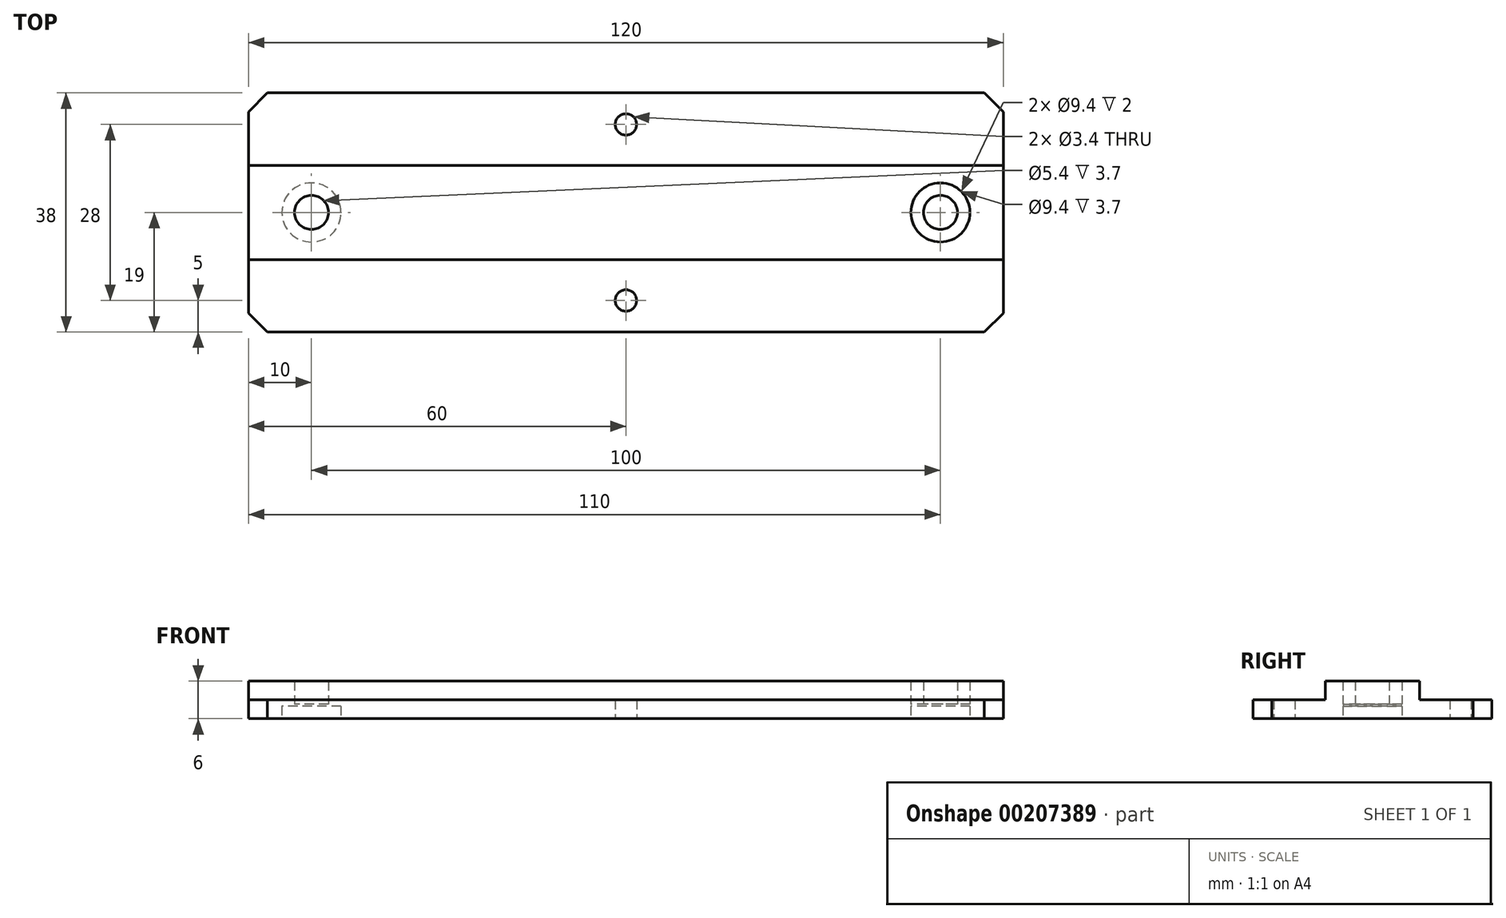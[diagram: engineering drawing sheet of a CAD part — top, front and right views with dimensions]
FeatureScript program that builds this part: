
annotation { "Feature Type Name" : "Feature", "Feature Type Description" : "" }
export const myFeature = defineFeature(function(context is Context, id is Id, definition is map)
    precondition{}
    {
        {
            var Q0;
            Q0=qCreatedBy(makeId("Top.planeOp"),FACE);
            var sketch = newSketch(context, id + "F0", { "sketchPlane" : qUnion([Q0])});
            skLineSegment(sketch, "E0.bottom", {"start": v(-12.5, 19) * mm, "end": v(12.5, 19) * mm});
            skLineSegment(sketch, "E0.top", {"start": v(-8.92, -19) * mm, "end": v(16.08, -19) * mm});
            skPoint(sketch, "E1", {"position": v(0, 19) * mm});
            skPoint(sketch, "E2.rect.middle", {"position": v(-50, 0) * mm});
            skCircle(sketch, "E3", {"center": v(-50, 0) * mm, "radius": 2.7 * mm});
            skCircle(sketch, "E4", {"center": v(-50, 0) * mm, "radius": 4.7 * mm});
            skLineSegment(sketch, "E5", {"start": v(-12.5, 7.5) * mm, "end": v(12.5, 7.5) * mm});
            skLineSegment(sketch, "E6", {"start": v(-12.5, -7.5) * mm, "end": v(12.5, -7.5) * mm});
            skPoint(sketch, "E7", {"position": v(12.5, 0) * mm});
            skLineSegment(sketch, "E8", {"start": v(5.33, 7.5) * mm, "end": v(5.33, -7.5) * mm, "construction": true});
            skPoint(sketch, "E9", {"position": v(5.33, 0) * mm});
            skCircle(sketch, "E10", {"center": v(0, 14) * mm, "radius": 1.7 * mm});
            skCircle(sketch, "E11", {"center": v(0, -14) * mm, "radius": 1.7 * mm});
            skLineSegment(sketch, "E12", {"start": v(0, 14) * mm, "end": v(0, 14) * mm});
            skLineSegment(sketch, "E13", {"start": v(-12.5, 19) * mm, "end": v(-60, 19) * mm});
            skLineSegment(sketch, "E14", {"start": v(-8.92, -19) * mm, "end": v(-60, -19) * mm});
            skLineSegment(sketch, "E15", {"start": v(-60, -19) * mm, "end": v(-60, 19) * mm});
            skLineSegment(sketch, "E16", {"start": v(-12.5, 7.5) * mm, "end": v(-60, 7.5) * mm});
            skLineSegment(sketch, "E17", {"start": v(-12.5, -7.5) * mm, "end": v(-60, -7.5) * mm});
            skLineSegment(sketch, "E18.MirrorCS", {"start": v(12.5, 19) * mm, "end": v(60, 19) * mm});
            skLineSegment(sketch, "E19.MirrorCS", {"start": v(12.5, 7.5) * mm, "end": v(60, 7.5) * mm});
            skLineSegment(sketch, "E20.MirrorCS", {"start": v(12.5, -7.5) * mm, "end": v(60, -7.5) * mm});
            skLineSegment(sketch, "E21.MirrorCS", {"start": v(60, -19) * mm, "end": v(60, 19) * mm});
            skLineSegment(sketch, "E22.MirrorCS", {"start": v(8.92, -19) * mm, "end": v(60, -19) * mm});
            skPoint(sketch, "E23.MirrorP", {"position": v(50, 0) * mm});
            skCircle(sketch, "E24.MirrorC", {"center": v(50, 0) * mm, "radius": 2.7 * mm});
            skCircle(sketch, "E25.MirrorC", {"center": v(50, 0) * mm, "radius": 4.7 * mm});
            skLineSegment(sketch, "E26", {"start": v(0, 7.5) * mm, "end": v(0, -7.5) * mm, "construction": true});
            skPoint(sketch, "E27", {"position": v(0, 0) * mm});
            skLineSegment(sketch, "E28", {"start": v(0, 14) * mm, "end": v(0, -14) * mm, "construction": true});
            skSolve(sketch);
        }
        {
            var Q0;
            Q0=makeQuery(id+"F0.imprint","IMPRINT",FACE,{"disambiguationData":[TD([[makeQuery(id+"F0.imprint","IMPRINT",EDGE,{"derivedFrom":sQuery(id+"F0.wireOp",EDGE,"E0.bottom")}),-1.0]])]});
            var Q1;
            {var subQ1=sQuery(id+"F0.wireOp",EDGE,"E0.top");Q1=makeQuery(id+"F0.imprint","IMPRINT",FACE,{"disambiguationData":[TD([[makeQuery(id+"F0.imprint","IMPRINT",EDGE,{"derivedFrom":subQ1}),1.0]])]});}
            extrude(context, id + "F1", {"entities" : qUnion([Q0, Q1]), "depth" : 3 * mm});
        }
        {
            var Q0;
            Q0=makeQuery(id+"F0.imprint","IMPRINT",FACE,{"disambiguationData":[TD([[makeQuery(id+"F0.imprint","IMPRINT",EDGE,{"derivedFrom":sQuery(id+"F0.wireOp",EDGE,"E4")}),-1.0]])]});
            var Q1;
            Q1=makeQuery(id+"F0.imprint","IMPRINT",FACE,{"disambiguationData":[TD([[makeQuery(id+"F0.imprint","IMPRINT",EDGE,{"derivedFrom":sQuery(id+"F0.wireOp",EDGE,"E3")}),-1.0]])]});
            var Q2;
            Q2=makeQuery(id+"F0.imprint","IMPRINT",FACE,{"disambiguationData":[TD([[makeQuery(id+"F0.imprint","IMPRINT",EDGE,{"derivedFrom":sQuery(id+"F0.wireOp",EDGE,"E24.MirrorC")}),1.0]])]});
            extrude(context, id + "F2", {"entities" : qUnion([Q0, Q1, Q2]), "operationType" : NewBodyOperationType.ADD, "depth" : 6 * mm});
        }
        {
            var Q0;
            Q0=makeQuery(id+"F0.imprint","IMPRINT",FACE,{"disambiguationData":[TD([[makeQuery(id+"F0.imprint","IMPRINT",EDGE,{"derivedFrom":sQuery(id+"F0.wireOp",EDGE,"E3")}),-1.0]])]});
            var Q1;
            Q1=makeQuery(id+"F0.imprint","IMPRINT",FACE,{"disambiguationData":[TD([[makeQuery(id+"F0.imprint","IMPRINT",EDGE,{"derivedFrom":sQuery(id+"F0.wireOp",EDGE,"E24.MirrorC")}),1.0]])]});
            extrude(context, id + "F3", {"entities" : qUnion([Q0, Q1]), "operationType" : NewBodyOperationType.REMOVE, "depth" : 2 * mm});
        }
        {
            var Q0;
            Q0=makeQuery(id+"F1.opExtrude","CAP_EDGE",EDGE,{"disambiguationData":[OSD([sQuery(id+"F0.wireOp",EDGE,"E5")])],"isStart":false});
            var Q1;
            Q1=makeQuery(id+"F1.opExtrude","CAP_EDGE",EDGE,{"disambiguationData":[OSD([sQuery(id+"F0.wireOp",EDGE,"E6")])],"isStart":false});
            var Q2;
            Q2=makeQuery(id+"F1.opExtrude","SWEPT_EDGE",EDGE,{"disambiguationData":[OSD([sQuery(id+"F0.wireOp",EDGE,"E0.top"),sQuery(id+"F0.wireOp",EDGE,"M45v7wsh-JOd0-Pyjo-Zry7-Q2iDr4y4sELp")])]});
            var Q3;
            Q3=makeQuery(id+"F1.opExtrude","SWEPT_EDGE",EDGE,{"disambiguationData":[OSD([sQuery(id+"F0.wireOp",EDGE,"E0.top"),sQuery(id+"F0.wireOp",EDGE,"0TBppSpT-un3e-81Sq-GRGt-UvVdAPZy041B")])]});
            var Q4;
            Q4=makeQuery(id+"F1.opExtrude","SWEPT_EDGE",EDGE,{"disambiguationData":[OSD([sQuery(id+"F0.wireOp",EDGE,"E0.bottom"),sQuery(id+"F0.wireOp",EDGE,"M45v7wsh-JOd0-Pyjo-Zry7-Q2iDr4y4sELp")])]});
            var Q5;
            Q5=makeQuery(id+"F1.opExtrude","SWEPT_EDGE",EDGE,{"disambiguationData":[OSD([sQuery(id+"F0.wireOp",EDGE,"E0.bottom"),sQuery(id+"F0.wireOp",EDGE,"0TBppSpT-un3e-81Sq-GRGt-UvVdAPZy041B")])]});
            var Q6;
            Q6=makeQuery(id+"F1.opExtrude","SWEPT_EDGE",EDGE,{"disambiguationData":[OSD([sQuery(id+"F0.wireOp",EDGE,"E14"),sQuery(id+"F0.wireOp",EDGE,"E15")])]});
            var Q7;
            Q7=makeQuery(id+"F1.opExtrude","SWEPT_EDGE",EDGE,{"disambiguationData":[OSD([sQuery(id+"F0.wireOp",EDGE,"E13"),sQuery(id+"F0.wireOp",EDGE,"E15")])]});
            var Q8;
            Q8=makeQuery(id+"F1.opExtrude","SWEPT_EDGE",EDGE,{"disambiguationData":[OSD([sQuery(id+"F0.wireOp",EDGE,"E21.MirrorCS"),sQuery(id+"F0.wireOp",EDGE,"E22.MirrorCS")])]});
            var Q9;
            Q9=makeQuery(id+"F1.opExtrude","SWEPT_EDGE",EDGE,{"disambiguationData":[OSD([sQuery(id+"F0.wireOp",EDGE,"E18.MirrorCS"),sQuery(id+"F0.wireOp",EDGE,"E21.MirrorCS")])]});
            chamfer(context, id + "F4", {"entities" : qUnion([Q0, Q1, Q2, Q3, Q4, Q5, Q6, Q7, Q8, Q9]), "width" : 3 * mm, "tangentPropagation" : true});
        }
        {
            var Q0;
            Q0=makeQuery(id+"F0.imprint","IMPRINT",FACE,{"disambiguationData":[TD([[makeQuery(id+"F0.imprint","IMPRINT",EDGE,{"derivedFrom":sQuery(id+"F0.wireOp",EDGE,"E3")}),1.0]])]});
            var Q1;
            Q1=makeQuery(id+"F0.imprint","IMPRINT",FACE,{"disambiguationData":[TD([[makeQuery(id+"F0.imprint","IMPRINT",EDGE,{"derivedFrom":sQuery(id+"F0.wireOp",EDGE,"E24.MirrorC")}),-1.0]])]});
            extrude(context, id + "F5", {"entities" : qUnion([Q0, Q1]), "operationType" : NewBodyOperationType.ADD, "depth" : 2.3 * mm, "hasSecondDirection" : true, "secondDirectionOppositeDirection" : false, "secondDirectionDepth" : 2 * mm});
        }
    });
